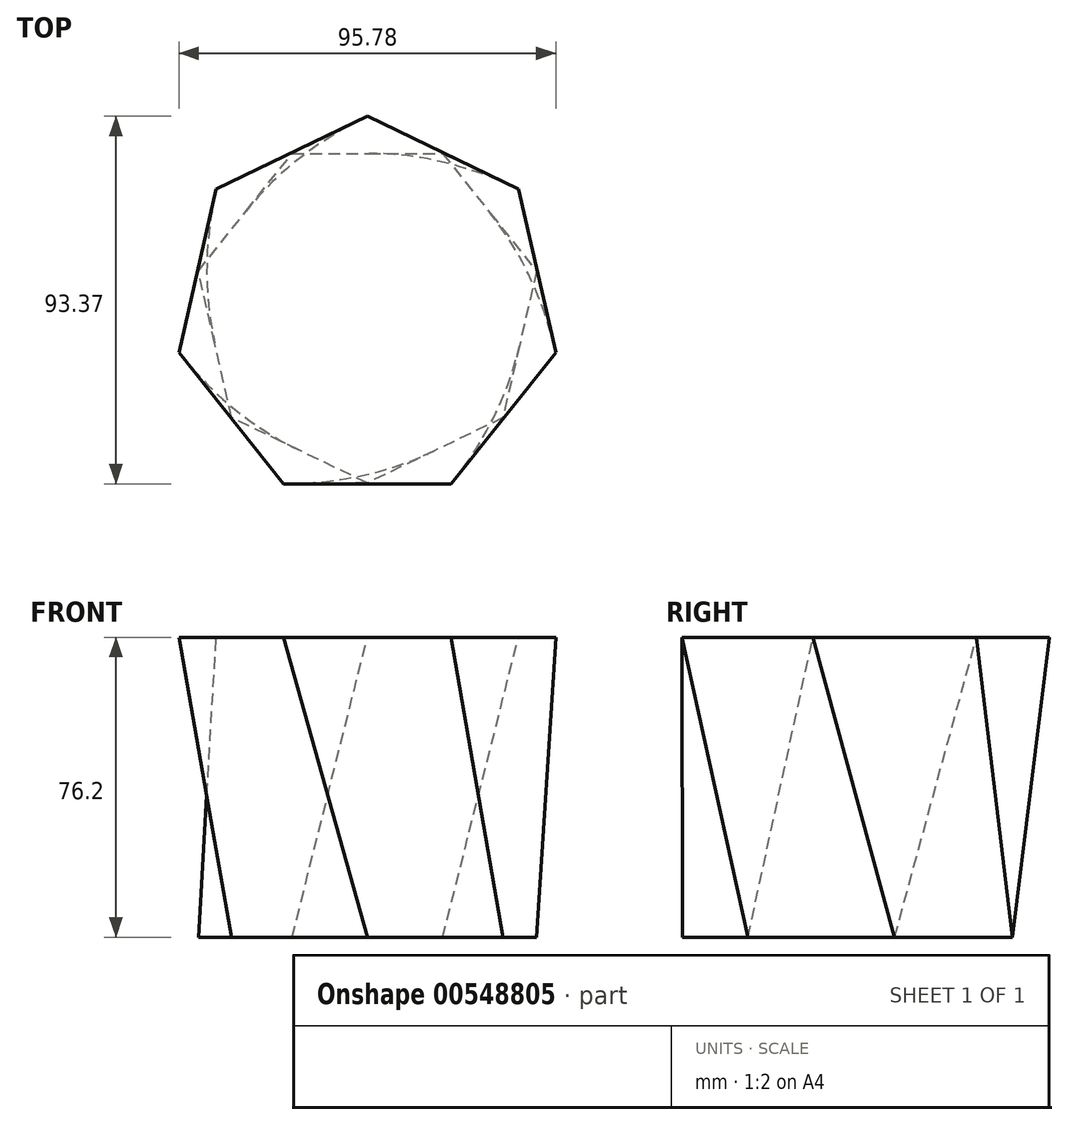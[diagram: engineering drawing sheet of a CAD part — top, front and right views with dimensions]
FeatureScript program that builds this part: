
annotation { "Feature Type Name" : "Feature", "Feature Type Description" : "" }
export const myFeature = defineFeature(function(context is Context, id is Id, definition is map)
    precondition{}
    {
        {
            var Q0;
            Q0=qCreatedBy(makeId("Top.planeOp"),FACE);
            var sketch = newSketch(context, id + "F0", { "sketchPlane" : qUnion([Q0])});
            skLineSegment(sketch, "E0", {"start": v(0, 0) * mm, "end": v(0, 39.69) * mm, "construction": true});
            skCircle(sketch, "E1.cCircle", {"center": v(0, 0) * mm, "radius": 39.69 * mm, "construction": true});
            skLineSegment(sketch, "E1.0", {"start": v(-19.11, 39.69) * mm, "end": v(19.11, 39.69) * mm});
            skLineSegment(sketch, "E1.1", {"start": v(19.11, 39.69) * mm, "end": v(42.95, 9.8) * mm});
            skLineSegment(sketch, "E1.2", {"start": v(42.95, 9.8) * mm, "end": v(34.44, -27.46) * mm});
            skLineSegment(sketch, "E1.3", {"start": v(34.44, -27.46) * mm, "end": v(0, -44.05) * mm});
            skLineSegment(sketch, "E1.4", {"start": v(0, -44.05) * mm, "end": v(-34.44, -27.46) * mm});
            skLineSegment(sketch, "E1.5", {"start": v(-34.44, -27.46) * mm, "end": v(-42.95, 9.8) * mm});
            skLineSegment(sketch, "E1.6", {"start": v(-42.95, 9.8) * mm, "end": v(-19.11, 39.69) * mm});
            skPoint(sketch, "E1.0.midPoint", {"position": v(0, 39.69) * mm});
            skSolve(sketch);
        }
        {
            var Q0;
            Q0=qCreatedBy(makeId("Top.planeOp"),FACE);
            cPlane(context, id + "F1", {"entities" : qUnion([Q0]), "cplaneType" : CPlaneType.OFFSET, "offset" : 76.2 * mm, "width" : 152.4 * mm, "height" : 152.4 * mm});
        }
        {
            var Q0;
            Q0=qCreatedBy(id+"F1.planeOp",FACE);
            var sketch = newSketch(context, id + "F2", { "sketchPlane" : qUnion([Q0])});
            skLineSegment(sketch, "E2", {"start": v(0, 0) * mm, "end": v(0, -44.25) * mm, "construction": true});
            skCircle(sketch, "E3.cCircle", {"center": v(0, 0) * mm, "radius": 44.25 * mm, "construction": true});
            skLineSegment(sketch, "E3.0", {"start": v(21.31, -44.25) * mm, "end": v(-21.31, -44.25) * mm});
            skLineSegment(sketch, "E3.1", {"start": v(-21.31, -44.25) * mm, "end": v(-47.89, -10.93) * mm});
            skLineSegment(sketch, "E3.2", {"start": v(-47.89, -10.93) * mm, "end": v(-38.4, 30.62) * mm});
            skLineSegment(sketch, "E3.3", {"start": v(-38.4, 30.62) * mm, "end": v(0, 49.12) * mm});
            skLineSegment(sketch, "E3.4", {"start": v(0, 49.12) * mm, "end": v(38.4, 30.62) * mm});
            skLineSegment(sketch, "E3.5", {"start": v(38.4, 30.62) * mm, "end": v(47.89, -10.93) * mm});
            skLineSegment(sketch, "E3.6", {"start": v(47.89, -10.93) * mm, "end": v(21.31, -44.25) * mm});
            skPoint(sketch, "E3.0.midPoint", {"position": v(0, -44.25) * mm});
            skSolve(sketch);
        }
        {
            var Q0;
            Q0=makeQuery(id+"F0.imprint","IMPRINT",FACE,{"disambiguationData":[TD([[makeQuery(id+"F0.imprint","IMPRINT",EDGE,{"derivedFrom":sQuery(id+"F0.wireOp",EDGE,"E1.0")}),-1.0]])]});
            var Q1;
            Q1=makeQuery(id+"F2.imprint","IMPRINT",FACE,{"disambiguationData":[TD([[makeQuery(id+"F2.imprint","IMPRINT",EDGE,{"derivedFrom":sQuery(id+"F2.wireOp",EDGE,"E3.0")}),-1.0]])]});
            loft(context, id + "F3", {"sheetProfilesArray" : [{ "sheetProfileEntities" : qUnion([Q0]) }, { "sheetProfileEntities" : qUnion([Q1]) }]});
        }
    });
